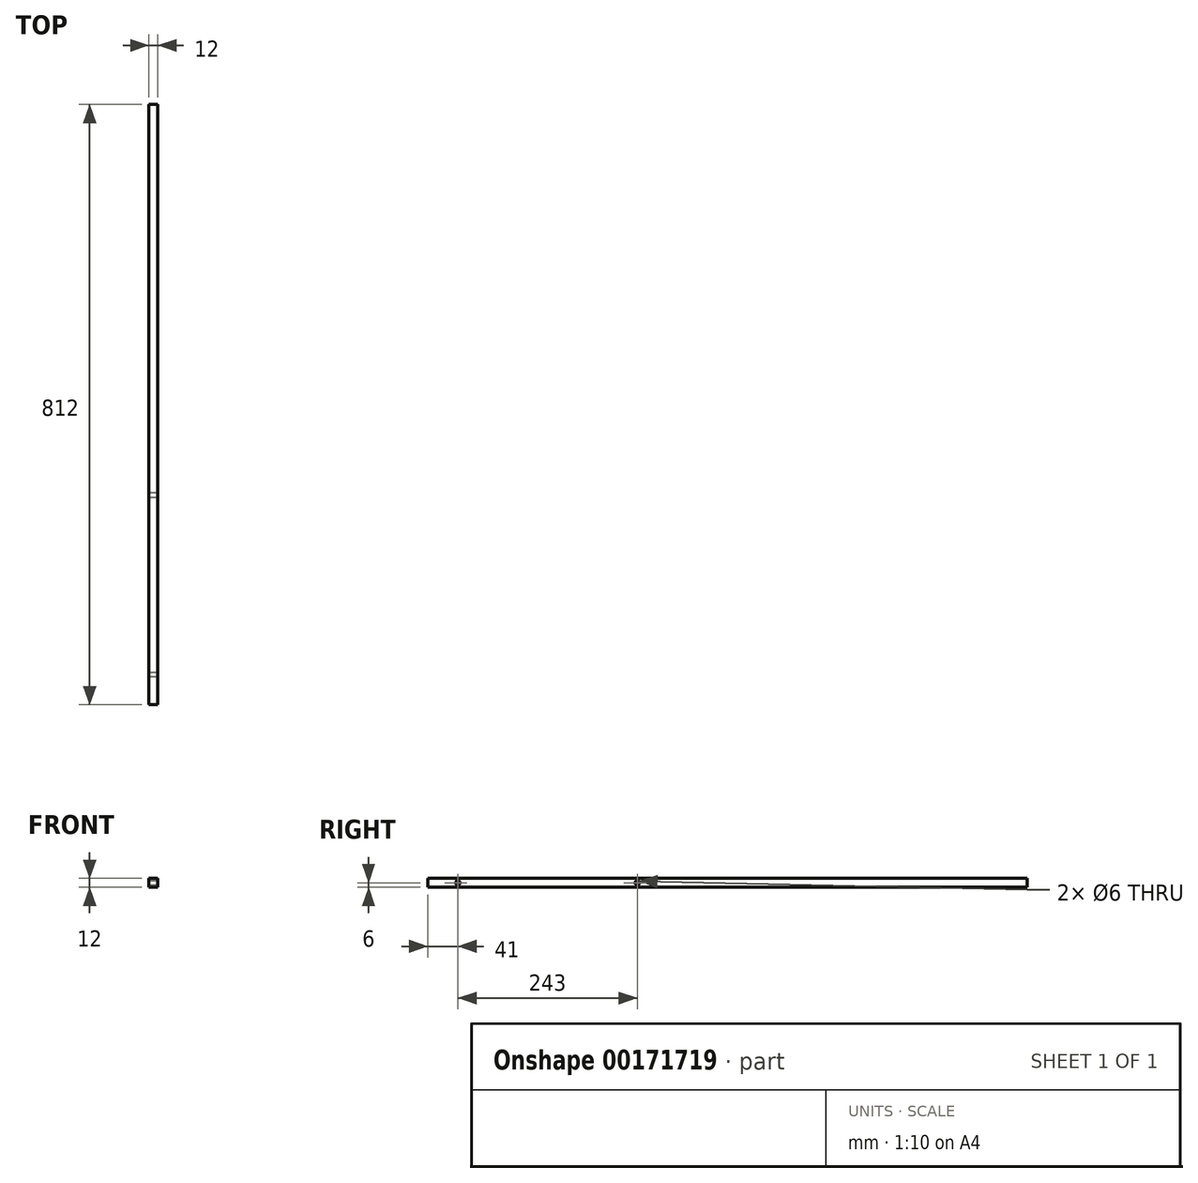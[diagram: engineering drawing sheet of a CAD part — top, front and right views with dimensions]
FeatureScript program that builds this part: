
annotation { "Feature Type Name" : "Feature", "Feature Type Description" : "" }
export const myFeature = defineFeature(function(context is Context, id is Id, definition is map)
    precondition{}
    {
        {
            var Q0;
            Q0=qCreatedBy(makeId("Front.planeOp"),FACE);
            var sketch = newSketch(context, id + "F0", { "sketchPlane" : qUnion([Q0])});
            skLineSegment(sketch, "E0.bottom", {"start": v(-6, 6) * mm, "end": v(6, 6) * mm});
            skLineSegment(sketch, "E0.top", {"start": v(-6, -6) * mm, "end": v(6, -6) * mm});
            skLineSegment(sketch, "E0.left", {"start": v(-6, 6) * mm, "end": v(-6, -6) * mm});
            skLineSegment(sketch, "E0.right", {"start": v(6, 6) * mm, "end": v(6, -6) * mm});
            skPoint(sketch, "E0.middle", {"position": v(0, 0) * mm});
            skSolve(sketch);
        }
        {
            var Q0;
            Q0=makeQuery(id+"F0.imprint","IMPRINT",FACE,{"disambiguationData":[TD([[makeQuery(id+"F0.imprint","IMPRINT",EDGE,{"derivedFrom":sQuery(id+"F0.wireOp",EDGE,"E0.bottom")}),-1.0]])]});
            extrude(context, id + "F1", {"entities" : qUnion([Q0]), "depth" : 812 * mm});
        }
        {
            var Q0;
            Q0=makeQuery(id+"F1.opExtrude","SWEPT_FACE",FACE,{"disambiguationData":[OSD([sQuery(id+"F0.wireOp",EDGE,"E0.right")])]});
            var sketch = newSketch(context, id + "F2", { "sketchPlane" : qUnion([Q0])});
            skPoint(sketch, "E1", {"position": v(-771, 0) * mm});
            skPoint(sketch, "E2", {"position": v(-528, 0) * mm});
            skSolve(sketch);
        }
        {
            var Q0;
            Q0=sQuery(id+"F2.wireOp",VERTEX,"E1");
            var Q1;
            Q1=sQuery(id+"F2.wireOp",VERTEX,"E2");
            var Q2;
            Q2=makeQuery(id+"F1.opExtrude","SWEPT_BODY",BODY,{"disambiguationData":[OSD([sQuery(id+"F0.wireOp",EDGE,"E0.bottom"),sQuery(id+"F0.wireOp",EDGE,"E0.top"),sQuery(id+"F0.wireOp",EDGE,"E0.left"),sQuery(id+"F0.wireOp",EDGE,"E0.right")])]});
            hole(context, id + "F3", {"style" : HoleStyle.C_SINK, "endStyle" : HoleEndStyle.BLIND, "holeDiameter" : 6 * mm, "cSinkDiameter" : 6 * mm, "cSinkAngle" : 90 * degree, "holeDepth" : 12 * mm, "startFromSketch" : true, "locations" : qUnion([Q0, Q1]), "scope" : qUnion([Q2])});
        }
    });
